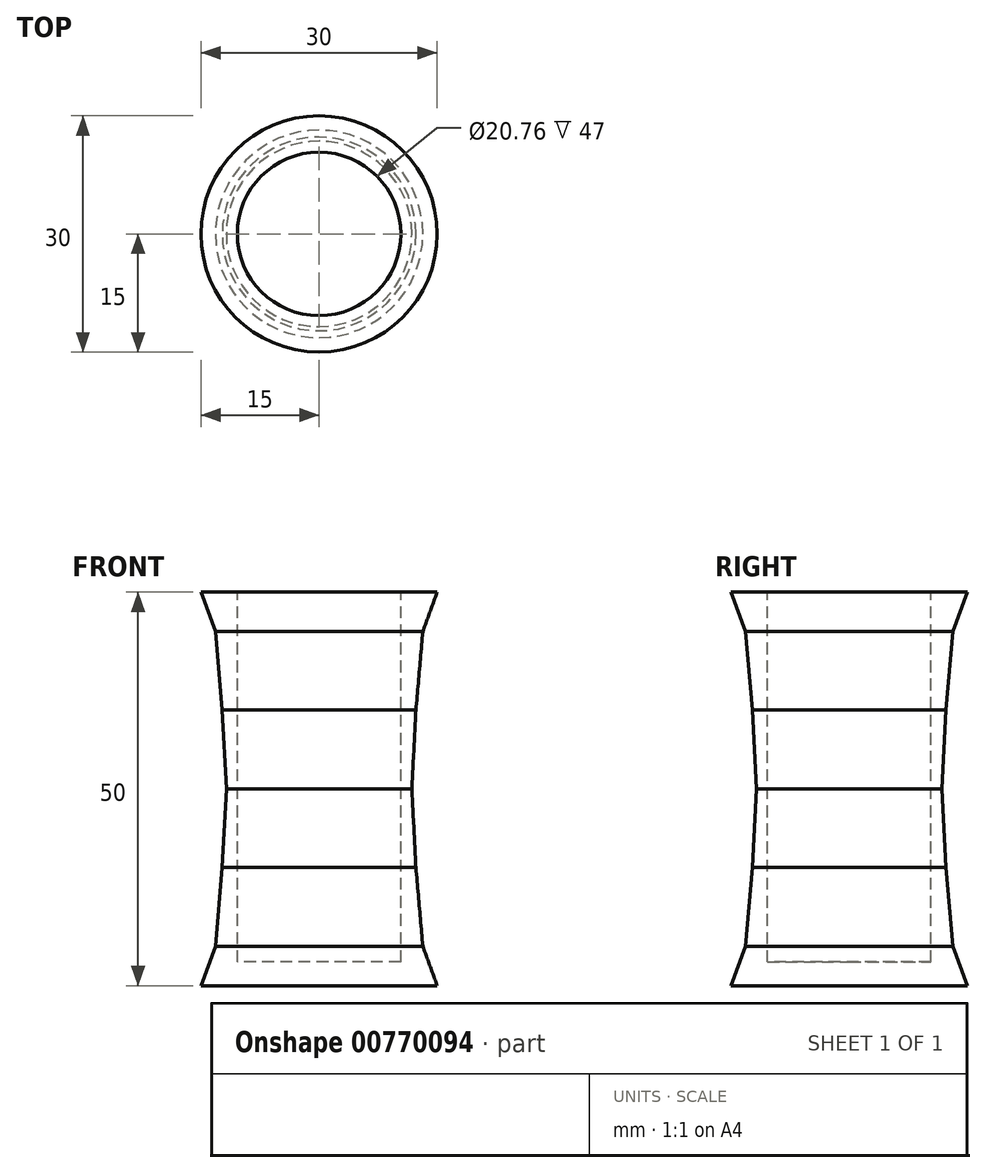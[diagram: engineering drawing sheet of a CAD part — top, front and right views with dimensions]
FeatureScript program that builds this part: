
annotation { "Feature Type Name" : "Feature", "Feature Type Description" : "" }
export const myFeature = defineFeature(function(context is Context, id is Id, definition is map)
    precondition{}
    {
        {
            var Q0;
            Q0=qCreatedBy(makeId("Top.planeOp"),FACE);
            var sketch = newSketch(context, id + "F0", { "sketchPlane" : qUnion([Q0])});
            skCircle(sketch, "E0", {"center": v(0, 0) * mm, "radius": 15 * mm});
            skSolve(sketch);
        }
        {
            var Q0;
            Q0=makeQuery(id+"F0.imprint","IMPRINT",FACE,{"disambiguationData":[TD([[makeQuery(id+"F0.imprint","IMPRINT",EDGE,{"derivedFrom":sQuery(id+"F0.wireOp",EDGE,"E0")}),1.0]])]});
            extrude(context, id + "F1", {"entities" : qUnion([Q0]), "depth" : 5 * mm, "offsetDistance" : 25 * mm, "hasDraft" : true, "draftAngle" : 20 * degree, "draftPullDirection" : true});
        }
        {
            var Q0;
            Q0=makeQuery(id+"F1.opExtrude","CAP_FACE",FACE,{"disambiguationData":[OSD([sQuery(id+"F0.wireOp",EDGE,"E0")])],"isStart":false});
            extrude(context, id + "F2", {"entities" : qUnion([Q0]), "operationType" : NewBodyOperationType.ADD, "depth" : 10 * mm, "offsetDistance" : 25 * mm, "hasDraft" : true, "draftAngle" : 5 * degree, "draftPullDirection" : true});
        }
        {
            var Q0;
            Q0=makeQuery(id+"F2.opExtrude","CAP_FACE",FACE,{"disambiguationData":[OSD([sQuery(id+"F0.wireOp",EDGE,"E0")])],"isStart":false});
            extrude(context, id + "F3", {"entities" : qUnion([Q0]), "operationType" : NewBodyOperationType.ADD, "depth" : 10 * mm, "offsetDistance" : 25 * mm, "hasDraft" : true, "draftAngle" : 3 * degree, "draftPullDirection" : true});
        }
        {
            var Q0;
            Q0=makeQuery(id+"F3.opExtrude","CAP_FACE",FACE,{"disambiguationData":[OSD([sQuery(id+"F0.wireOp",EDGE,"E0")])],"isStart":false});
            extrude(context, id + "F4", {"entities" : qUnion([Q0]), "operationType" : NewBodyOperationType.ADD, "depth" : 10 * mm, "offsetDistance" : 25 * mm, "hasDraft" : true, "draftAngle" : 3 * degree});
        }
        {
            var Q0;
            Q0=makeQuery(id+"F4.opExtrude","CAP_FACE",FACE,{"disambiguationData":[OSD([sQuery(id+"F0.wireOp",EDGE,"E0")])],"isStart":false});
            extrude(context, id + "F5", {"entities" : qUnion([Q0]), "operationType" : NewBodyOperationType.ADD, "depth" : 10 * mm, "offsetDistance" : 25 * mm, "hasDraft" : true, "draftAngle" : 5 * degree});
        }
        {
            var Q0;
            Q0=makeQuery(id+"F5.opExtrude","CAP_FACE",FACE,{"disambiguationData":[OSD([sQuery(id+"F0.wireOp",EDGE,"E0")])],"isStart":false});
            extrude(context, id + "F6", {"entities" : qUnion([Q0]), "operationType" : NewBodyOperationType.ADD, "depth" : 5 * mm, "offsetDistance" : 25 * mm, "hasDraft" : true, "draftAngle" : 20 * degree});
        }
        {
            var Q0;
            Q0=makeQuery(id+"F6.opExtrude","CAP_FACE",FACE,{"disambiguationData":[OSD([sQuery(id+"F0.wireOp",EDGE,"E0")])],"isStart":false});
            var sketch = newSketch(context, id + "F7", { "sketchPlane" : qUnion([Q0])});
            skCircle(sketch, "E1", {"center": v(0, 0) * mm, "radius": 10.38 * mm});
            skSolve(sketch);
        }
        {
            var Q0;
            Q0 = qSketchRegion(id + "F7", true);
            extrude(context, id + "F8", {"entities" : qUnion([Q0]), "operationType" : NewBodyOperationType.REMOVE, "depth" : -47 * mm, "offsetDistance" : 25 * mm});
        }
    });
